# Revit family: NBS_Allermuir_DmstcChrs_Mote-en-us_MTEMEDTB12
name_source: partatom
category: Furniture
revit_build: Autodesk Revit 2016 (Build: 20151007_0715(x64)
units: mm (PartAtom-declared; Revit-internal decimal feet)

## family parameters
Always vertical = Yes
Cut with Voids When Loaded = No
Room Calculation Point = No
Shared = No
Work Plane-Based = No

## types (1)
- MTEMEDTB12
    AssetType = Moveable
    BIMObjectName = NBS_Allermuir_DomesticChairs_Mote_MTEMEDTB12-US
    Category = Pr_40_50_12_22:Dining chairs
    ColumnMaterial = NBS_Concept
    Description = Four/six seat table
    DurationUnit = year
    ExpectedLife = 10
    Features = 1" TFL top with a clear edge profile, available in all standard TFL, fully upholstered table support in fabric matching bridging screen, table support base plate finished in black powder coat, plastic glides, table support base plate available in flint grey, mineral sand, mellow yellow or orange crush powder coat, table edge profile can be stained
    FootHeight = 0 "
    FrameColourOptions = Flint grey, mineral sand, mellow yellow or orange crush
    FrameMountingMaterial = NBS_Concept
    FrameShroudMaterial = NBS_Concept
    FramesColour = Black
    FramesFinish = Powder coat
    HighestSeatingHeight = 0 "
    IfcExportAs = IfcFurnitureType
    IfcExportType = SOFA
    IsBuiltIn = No
    LowestSeatingHeight = 0 "
    ManufacturerName = Allermuir
    ManufacturerURL = http://www.thesenatorgroup.com
    ModelNumber = MTEMEDTB12
    ModelReference = Mote accessories
    NBSCertification = www.nationalbimlibrary.com/cert/lbow5utl
    NBSDescription = Domestic chairs
    NBSReference = 45-35-20/365
    Name = DomesticChairs_Mote_MTE-MEDTB12-US_Allermuir
    NominalDepth = 31 "
    NominalHeight = 29 "
    NominalLength = 53 "
    NominalWidth = 31 "
    NumberOfChairs = 0
    OmniClassCode = 22-12 52 23
    OmniClassTitle = Office Seating
    OmniClassVersion = Table 22 2012-05-16
    PostHeight = 22 "
    ProductInformation = http://www.thesenatorgroup.com
    SeatingHeight = 0 "
    SeatsAndBacksMaterial = Upholstered
    Size = 33.5 x 29 x 53.25"
    Status = UNSET
    TableTopLength = 53 "
    TableTopSupportRailMaterial = NBS_Concept
    TableTopWidth = 31 "
    Uniclass2015Code = Pr_40_50_12_22
    Uniclass2015Title = Dining chairs
    Uniclass2015Version = Products v1.9
    Version = 1
    WarrantyDescription = Allermuir warrant that its manufactured products are free from manufacturing defects in materials or workmanship for a period of ten years
    WarrantyDurationParts = 10
    WarrantyDurationUnit = year
    WorksurfaceArea = 0 m²
    WorktopHeight = 29 "
    WorktopMFMDF = Yes
    WorktopMaterial = NBS_Concept
    WorktopMaterialTapedEdge = NBS_Concept
    WorktopThickness = 1 "
    WorktopType = NBS_Allermuir_DmstcChrs_Mote_MTE-MEDTB12MFMDF : MTE-MEDTB12MFMDF

## geometry (parser evidence)
native form markers: Sweep x6
no freeform markers — native parametric forms only
